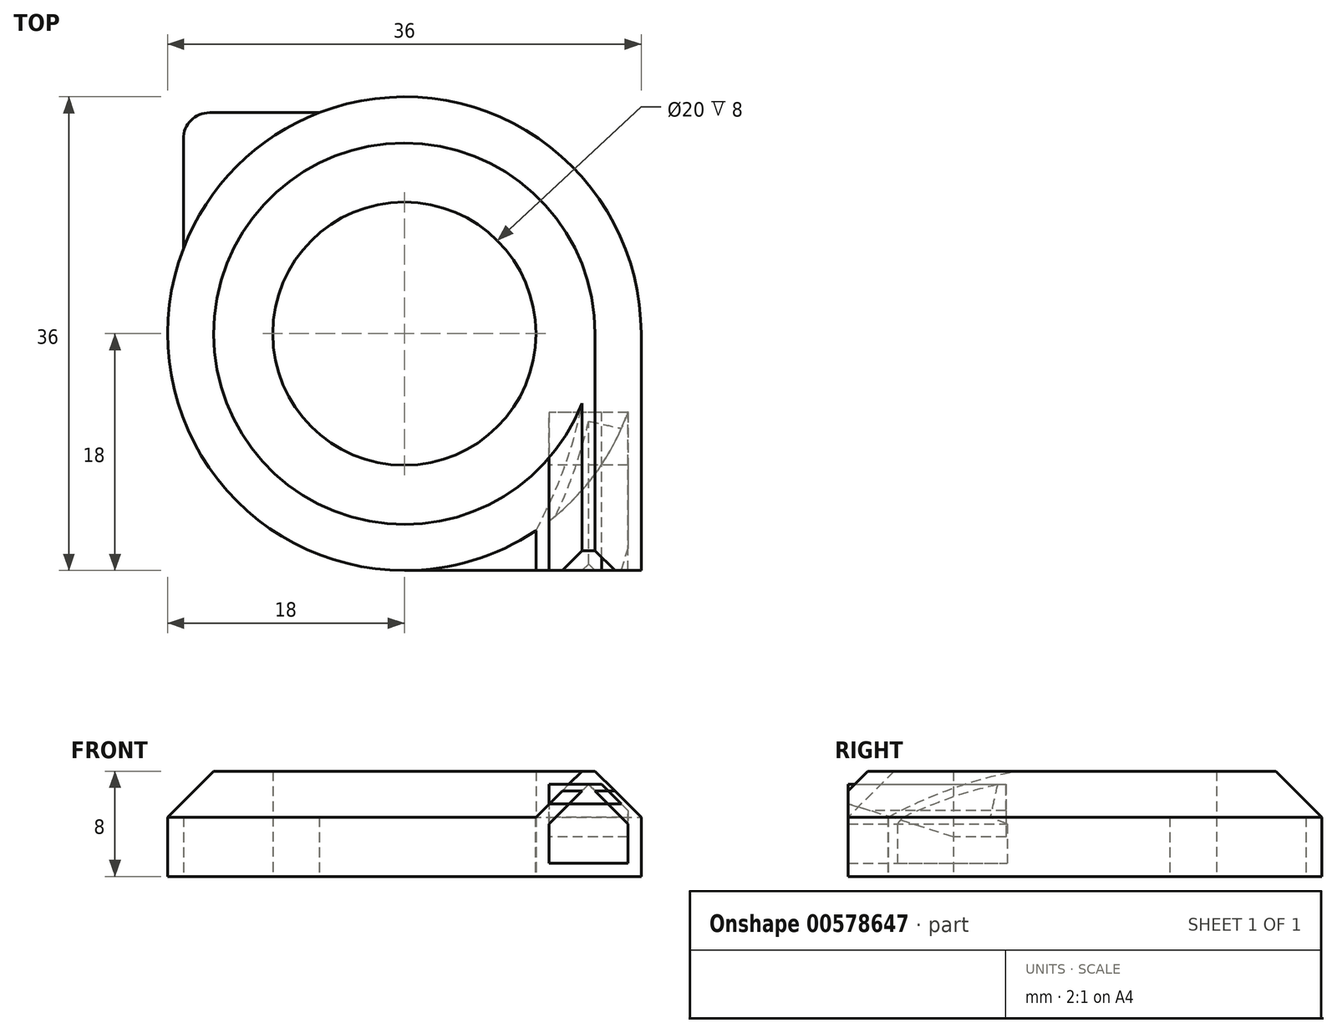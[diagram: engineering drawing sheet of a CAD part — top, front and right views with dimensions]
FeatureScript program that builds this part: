
annotation { "Feature Type Name" : "Feature", "Feature Type Description" : "" }
export const myFeature = defineFeature(function(context is Context, id is Id, definition is map)
    precondition{}
    {
        {
            var Q0;
            Q0=qCreatedBy(makeId("Front.planeOp"),FACE);
            var sketch = newSketch(context, id + "F0", { "sketchPlane" : qUnion([Q0])});
            skLineSegment(sketch, "E0", {"start": v(18, 0) * mm, "end": v(18, 4.5) * mm});
            skLineSegment(sketch, "E1", {"start": v(18, 4.5) * mm, "end": v(14.5, 8) * mm});
            skLineSegment(sketch, "E2", {"start": v(14.5, 8) * mm, "end": v(10, 8) * mm});
            skLineSegment(sketch, "E3", {"start": v(10, 8) * mm, "end": v(10, 0) * mm});
            skLineSegment(sketch, "E4", {"start": v(10, 0) * mm, "end": v(18, 0) * mm});
            skSolve(sketch);
        }
        {
            var Q0;
            Q0=qCreatedBy(makeId("Front.planeOp"),FACE);
            var sketch = newSketch(context, id + "F1", { "sketchPlane" : qUnion([Q0])});
            skLineSegment(sketch, "E5", {"start": v(18, 0) * mm, "end": v(18, 4.5) * mm});
            skLineSegment(sketch, "E6", {"start": v(18, 4.5) * mm, "end": v(14.5, 8) * mm});
            skLineSegment(sketch, "E7", {"start": v(14.5, 8) * mm, "end": v(10, 8) * mm});
            skLineSegment(sketch, "E8", {"start": v(10, 8) * mm, "end": v(10, 0) * mm});
            skLineSegment(sketch, "E9", {"start": v(10, 0) * mm, "end": v(18, 0) * mm});
            skSolve(sketch);
        }
        {
            var Q0;
            Q0=qCreatedBy(makeId("Front.planeOp"),FACE);
            var sketch = newSketch(context, id + "F2", { "sketchPlane" : qUnion([Q0])});
            skLineSegment(sketch, "E10", {"start": v(11, 1) * mm, "end": v(17, 1) * mm});
            skLineSegment(sketch, "E11", {"start": v(17, 1) * mm, "end": v(17, 4) * mm});
            skLineSegment(sketch, "E12", {"start": v(17, 4) * mm, "end": v(14.07, 7) * mm});
            skLineSegment(sketch, "E13", {"start": v(14.07, 7) * mm, "end": v(11, 4) * mm});
            skLineSegment(sketch, "E14", {"start": v(11, 4) * mm, "end": v(11, 1) * mm});
            skSolve(sketch);
        }
        {
            var Q0;
            Q0=qCreatedBy(makeId("Front.planeOp"),FACE);
            var sketch = newSketch(context, id + "F3", { "sketchPlane" : qUnion([Q0])});
            skLineSegment(sketch, "E15", {"start": v(11, 1) * mm, "end": v(17, 1) * mm});
            skLineSegment(sketch, "E16", {"start": v(17, 1) * mm, "end": v(17, 4) * mm});
            skLineSegment(sketch, "E17", {"start": v(17, 4) * mm, "end": v(14, 7) * mm});
            skLineSegment(sketch, "E18", {"start": v(14, 7) * mm, "end": v(11, 4) * mm});
            skLineSegment(sketch, "E19", {"start": v(11, 4) * mm, "end": v(11, 1) * mm});
            skSolve(sketch);
        }
        {
            var Q0;
            Q0=qCreatedBy(makeId("Top.planeOp"),FACE);
            var sketch = newSketch(context, id + "F4", { "sketchPlane" : qUnion([Q0])});
            skCircle(sketch, "E20", {"center": v(0, 0) * mm, "radius": 10 * mm});
            skSolve(sketch);
        }
        {
            var Q0;
            Q0 = qSketchRegion(id + "F0", true);
            var Q1;
            Q1=sQuery(id+"F4.wireOp",EDGE,"E20");
            revolve(context, id + "F5", {"entities" : qUnion([Q0]), "axis" : qUnion([Q1]), "revolveType" : RevolveType.FULL});
        }
        {
            var Q0;
            Q0=qCreatedBy(makeId("Top.planeOp"),FACE);
            var sketch = newSketch(context, id + "F6", { "sketchPlane" : qUnion([Q0])});
            skLineSegment(sketch, "E21", {"start": v(-14.8, 16.8) * mm, "end": v(-6, 16.8) * mm});
            skLineSegment(sketch, "E22", {"start": v(-6, 16.8) * mm, "end": v(-16.8, 6) * mm});
            skLineSegment(sketch, "E23", {"start": v(-16.8, 6) * mm, "end": v(-16.8, 14.8) * mm});
            skPoint(sketch, "E24.visualSharp", {"position": v(-16.8, 16.8) * mm});
            skArc(sketch, "E24.filletArc", {"start": v(-14.8, 16.8) * mm, "mid": v(-16.21, 16.21) * mm, "end": v(-16.8, 14.8) * mm});
            skSolve(sketch);
        }
        {
            var Q0;
            Q0 = qSketchRegion(id + "F1", true);
            extrude(context, id + "F7", {"entities" : qUnion([Q0]), "depth" : 18 * mm, "offsetDistance" : 25 * mm});
        }
        {
            var Q0;
            Q0 = qSketchRegion(id + "F2", true);
            var Q1;
            Q1=sQuery(id+"F4.wireOp",EDGE,"E20");
            revolve(context, id + "F8", {"entities" : qUnion([Q0]), "axis" : qUnion([Q1]), "revolveType" : RevolveType.ONE_DIRECTION, "angle" : 270 * degree});
        }
        {
            var Q0;
            Q0 = qSketchRegion(id + "F3", true);
            extrude(context, id + "F9", {"entities" : qUnion([Q0]), "depth" : 18 * mm, "offsetDistance" : 25 * mm});
        }
        {
            var Q0;
            Q0=makeQuery(id+"F8.opRevolve","SWEPT_BODY",BODY,{"disambiguationData":[OSD([sQuery(id+"F2.wireOp",EDGE,"E10"),sQuery(id+"F2.wireOp",EDGE,"E11"),sQuery(id+"F2.wireOp",EDGE,"E12"),sQuery(id+"F2.wireOp",EDGE,"E13"),sQuery(id+"F2.wireOp",EDGE,"E14")])]});
            var Q1;
            Q1=makeQuery(id+"F7.opExtrude","SWEPT_BODY",BODY,{"disambiguationData":[OSD([sQuery(id+"F1.wireOp",EDGE,"E5"),sQuery(id+"F1.wireOp",EDGE,"E6"),sQuery(id+"F1.wireOp",EDGE,"E7"),sQuery(id+"F1.wireOp",EDGE,"E8"),sQuery(id+"F1.wireOp",EDGE,"E9")])]});
            booleanBodies(context, id + "F10", {"operationType" : BooleanOperationType.SUBTRACTION, "tools" : qUnion([Q0]), "targets" : qUnion([Q1])});
        }
        {
            var Q0;
            Q0=makeQuery(id+"F9.opExtrude","SWEPT_BODY",BODY,{"disambiguationData":[OSD([sQuery(id+"F3.wireOp",EDGE,"E15"),sQuery(id+"F3.wireOp",EDGE,"E16"),sQuery(id+"F3.wireOp",EDGE,"E17"),sQuery(id+"F3.wireOp",EDGE,"E18"),sQuery(id+"F3.wireOp",EDGE,"E19")])]});
            var Q1;
            Q1=makeQuery(id+"F7.opExtrude","SWEPT_BODY",BODY,{"disambiguationData":[OSD([sQuery(id+"F1.wireOp",EDGE,"E5"),sQuery(id+"F1.wireOp",EDGE,"E6"),sQuery(id+"F1.wireOp",EDGE,"E7"),sQuery(id+"F1.wireOp",EDGE,"E8"),sQuery(id+"F1.wireOp",EDGE,"E9")])]});
            booleanBodies(context, id + "F11", {"operationType" : BooleanOperationType.SUBTRACTION, "tools" : qUnion([Q0]), "targets" : qUnion([Q1])});
        }
        {
            var Q0;
            Q0=qCreatedBy(makeId("Right.planeOp"),FACE);
            cPlane(context, id + "F12", {"entities" : qUnion([Q0]), "cplaneType" : CPlaneType.OFFSET, "offset" : 11 * mm, "width" : 150 * mm, "height" : 150 * mm});
        }
        {
            var Q0;
            Q0=qCreatedBy(id+"F12.planeOp",FACE);
            var sketch = newSketch(context, id + "F13", { "sketchPlane" : qUnion([Q0])});
            skLineSegment(sketch, "E25", {"start": v(-18, 7) * mm, "end": v(-6, 7) * mm});
            skLineSegment(sketch, "E26", {"start": v(-6, 7) * mm, "end": v(-6, 3) * mm});
            skLineSegment(sketch, "E27", {"start": v(-6, 3) * mm, "end": v(-10, 3) * mm});
            skLineSegment(sketch, "E28", {"start": v(-10, 3) * mm, "end": v(-18, 5.53) * mm});
            skLineSegment(sketch, "E29", {"start": v(-18, 5.53) * mm, "end": v(-18, 7) * mm});
            skSolve(sketch);
        }
        {
            var Q0;
            Q0=qCreatedBy(id+"F12.planeOp",FACE);
            var sketch = newSketch(context, id + "F14", { "sketchPlane" : qUnion([Q0])});
            skLineSegment(sketch, "E30", {"start": v(-6, 2) * mm, "end": v(-6, -1) * mm});
            skLineSegment(sketch, "E31", {"start": v(-6, -1) * mm, "end": v(1, -1) * mm});
            skLineSegment(sketch, "E32", {"start": v(1, -1) * mm, "end": v(-6, 2) * mm});
            skSolve(sketch);
        }
        {
            var Q0;
            Q0=makeQuery(id+"F13.imprint","IMPRINT",FACE,{"disambiguationData":[TD([[makeQuery(id+"F13.imprint","IMPRINT",EDGE,{"derivedFrom":sQuery(id+"F13.wireOp",EDGE,"E25")}),-1.0]])]});
            extrude(context, id + "F15", {"entities" : qUnion([Q0]), "depth" : 6 * mm, "offsetDistance" : 25 * mm});
        }
        {
            var Q0;
            Q0=makeQuery(id+"F14.imprint","IMPRINT",FACE,{"disambiguationData":[TD([[makeQuery(id+"F14.imprint","IMPRINT",EDGE,{"derivedFrom":sQuery(id+"F14.wireOp",EDGE,"E30")}),1.0]])]});
            extrude(context, id + "F16", {"entities" : qUnion([Q0]), "depth" : 7 * mm, "offsetDistance" : 25 * mm, "hasSecondDirection" : true, "secondDirectionOppositeDirection" : true, "secondDirectionDepth" : 1 * mm});
        }
        {
            var Q0;
            Q0=makeQuery(id+"F15.opExtrude","CAP_EDGE",EDGE,{"disambiguationData":[OSD([sQuery(id+"F13.wireOp",EDGE,"E25")])],"isStart":false});
            chamfer(context, id + "F17", {"entities" : qUnion([Q0]), "width" : 2 * mm, "tangentPropagation" : true});
        }
        {
            var Q0;
            Q0=makeQuery(id+"F16.opExtrude","SWEPT_BODY",BODY,{"disambiguationData":[OSD([sQuery(id+"F14.wireOp",EDGE,"E30"),sQuery(id+"F14.wireOp",EDGE,"E31"),sQuery(id+"F14.wireOp",EDGE,"E32")])]});
            var Q1;
            Q1=makeQuery(id+"F15.opExtrude","SWEPT_BODY",BODY,{"disambiguationData":[OSD([sQuery(id+"F13.wireOp",EDGE,"E25"),sQuery(id+"F13.wireOp",EDGE,"E26"),sQuery(id+"F13.wireOp",EDGE,"E27"),sQuery(id+"F13.wireOp",EDGE,"E28"),sQuery(id+"F13.wireOp",EDGE,"E29")])]});
            booleanBodies(context, id + "F18", {"operationType" : BooleanOperationType.SUBTRACTION, "tools" : qUnion([Q0]), "targets" : qUnion([Q1])});
        }
        {
            var Q0;
            Q0=qCreatedBy(makeId("Top.planeOp"),FACE);
            var sketch = newSketch(context, id + "F19", { "sketchPlane" : qUnion([Q0])});
            skCircle(sketch, "E33", {"center": v(-13.8, 13.8) * mm, "radius": 1.5 * mm});
            skSolve(sketch);
        }
        {
            var Q0;
            Q0=makeQuery(id+"F6.imprint","IMPRINT",FACE,{"disambiguationData":[TD([[makeQuery(id+"F6.imprint","IMPRINT",EDGE,{"derivedFrom":sQuery(id+"F6.wireOp",EDGE,"E21")}),-1.0]])]});
            extrude(context, id + "F20", {"entities" : qUnion([Q0]), "operationType" : NewBodyOperationType.ADD, "depth" : 4.5 * mm, "offsetDistance" : 25 * mm});
        }
        {
            var Q0;
            Q0 = qSketchRegion(id + "F19", true);
            extrude(context, id + "F21", {"entities" : qUnion([Q0]), "depth" : 5 * mm, "offsetDistance" : 25 * mm});
        }
        {
            var Q0;
            Q0=makeQuery(id+"F21.opExtrude","SWEPT_BODY",BODY,{"disambiguationData":[OSD([sQuery(id+"F19.wireOp",EDGE,"E33")])]});
            var Q1;
            Q1=makeQuery(id+"F15.opExtrude","SWEPT_BODY",BODY,{"disambiguationData":[OSD([sQuery(id+"F13.wireOp",EDGE,"E25"),sQuery(id+"F13.wireOp",EDGE,"E26"),sQuery(id+"F13.wireOp",EDGE,"E27"),sQuery(id+"F13.wireOp",EDGE,"E28"),sQuery(id+"F13.wireOp",EDGE,"E29")])]});
            booleanBodies(context, id + "F22", {"operationType" : BooleanOperationType.SUBTRACTION, "tools" : qUnion([Q0]), "targets" : qUnion([Q1])});
        }
        {
            var Q0;
            Q0=qCreatedBy(makeId("Top.planeOp"),FACE);
            var sketch = newSketch(context, id + "F23", { "sketchPlane" : qUnion([Q0])});
            skLineSegment(sketch, "E34.bottom", {"start": v(-0.01, -15) * mm, "end": v(11, -15) * mm});
            skLineSegment(sketch, "E34.top", {"start": v(-0.01, -18) * mm, "end": v(11, -18) * mm});
            skLineSegment(sketch, "E34.left", {"start": v(-0.01, -15) * mm, "end": v(-0.01, -18) * mm});
            skLineSegment(sketch, "E34.right", {"start": v(11, -15) * mm, "end": v(11, -18) * mm});
            skSolve(sketch);
        }
        {
            var Q0;
            Q0=makeQuery(id+"F23.imprint","IMPRINT",FACE,{"disambiguationData":[TD([[makeQuery(id+"F23.imprint","IMPRINT",EDGE,{"derivedFrom":sQuery(id+"F23.wireOp",EDGE,"E34.bottom")}),-1.0]])]});
            extrude(context, id + "F24", {"entities" : qUnion([Q0]), "operationType" : NewBodyOperationType.ADD, "depth" : 4.5 * mm, "offsetDistance" : 25 * mm});
        }
        {
            var Q0;
            Q0=makeQuery(id+"F7.opExtrude","SWEPT_EDGE",EDGE,{"disambiguationData":[OSD([sQuery(id+"F1.wireOp",EDGE,"E7"),sQuery(id+"F1.wireOp",EDGE,"E8")])]});
            chamfer(context, id + "F25", {"entities" : qUnion([Q0]), "width" : 3.5 * mm, "tangentPropagation" : true});
        }
        {
            var Q0;
            Q0=makeQuery(id+"F7.opExtrude","CAP_EDGE",EDGE,{"disambiguationData":[OSD([sQuery(id+"F1.wireOp",EDGE,"E7")])],"isStart":false});
            chamfer(context, id + "F26", {"entities" : qUnion([Q0]), "width" : 1.5 * mm, "tangentPropagation" : true});
        }
    });
